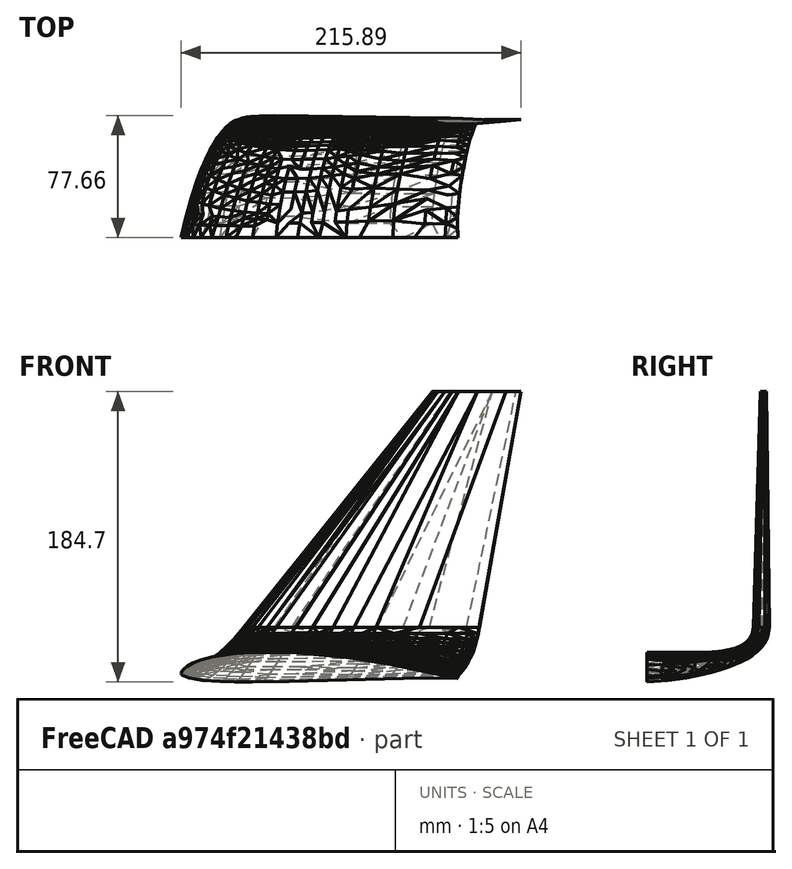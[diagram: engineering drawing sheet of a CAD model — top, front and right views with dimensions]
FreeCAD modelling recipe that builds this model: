
FCSTD DOCUMENT  (FreeCAD 0.19R24276 (Git))
Label: Con_right_winglet_default
License: All rights reserved
LicenseURL: http://en.wikipedia.org/wiki/All_rights_reserved
objects: Mesh::Feature×1, Part::Feature×1, Sketcher::SketchObject×1, PartDesign::Body×1
note: 3 computed .brp shape members not serialized (recipe doc carries the construction recipe); baked Part::Feature solids carry a one-line shape summary decoded from their .brp

FEATURE [Mesh::Feature] Con_right_winglet_default
FEATURE [Part::Feature] Con_right_winglet_default001
  shape: bbox 215.9 x 77.66 x 184.7 mm, 1678 faces, 0 solids (baked)
FEATURE [Sketcher::SketchObject] Sketch
  FullyConstrained = true
  MapMode = 5
  Placement = pos=(0,0,0) rot=(1,0,0;1.5708rad)
  Support = -> [XZ_Plane]
  sketch-geometry (8):
    g0: LineSegment StartX=100 StartY=260 StartZ=0 EndX=425 EndY=260 EndZ=0
    g1: LineSegment StartX=425 StartY=260 StartZ=0 EndX=425 EndY=60 EndZ=0
    g2: LineSegment StartX=425 StartY=60 StartZ=0 EndX=100 EndY=60 EndZ=0
    g3: LineSegment StartX=100 StartY=60 StartZ=0 EndX=100 EndY=260 EndZ=0
    g4: LineSegment StartX=100 StartY=50 StartZ=0 EndX=425 EndY=50 EndZ=0
    g5: LineSegment StartX=425 StartY=50 StartZ=0 EndX=425 EndY=0 EndZ=0
    g6: LineSegment StartX=425 StartY=0 StartZ=0 EndX=100 EndY=0 EndZ=0
    g7: LineSegment StartX=100 StartY=0 StartZ=0 EndX=100 EndY=50 EndZ=0
  constraints (24):
    c: Coincident(g0,g1)
    c: Coincident(g1,g2)
    c: Coincident(g2,g3)
    c: Coincident(g3,g0)
    c: Horizontal(g0)
    c: Horizontal(g2)
    c: Vertical(g1)
    c: Vertical(g3)
    c: DistanceX(g-1,g2) = 100
    c: DistanceX(g2,g2) = 325
    c: DistanceY(g3,g3) = 200
    c: DistanceY(g-1,g2) = 60
    c: Coincident(g4,g5)
    c: Coincident(g5,g6)
    c: Coincident(g6,g7)
    c: Coincident(g7,g4)
    c: Horizontal(g4)
    c: Horizontal(g6)
    c: Vertical(g5)
    c: Vertical(g7)
    c: PointOnObject(g6,g-1)
    c: DistanceX(g-1,g4) = 100
    c: DistanceX(g6,g6) = 325
    c: DistanceY(g5,g5) = 50
FEATURE [PartDesign::Body] Body
  Group = -> [Sketch]
  Origin = -> Origin
